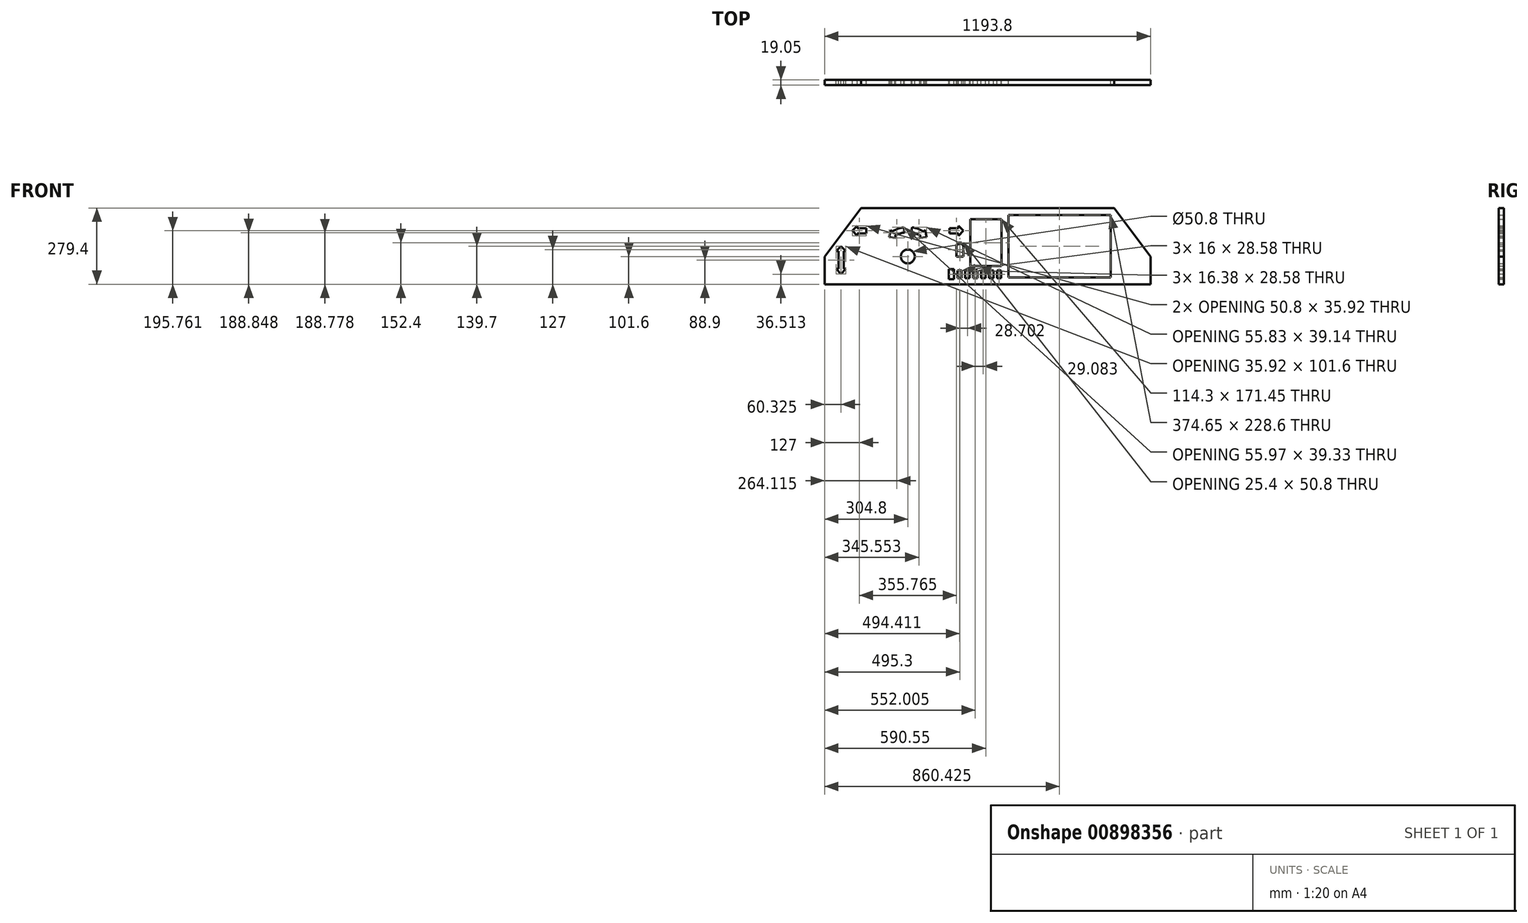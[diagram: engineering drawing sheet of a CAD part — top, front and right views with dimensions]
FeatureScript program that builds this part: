
annotation { "Feature Type Name" : "Feature", "Feature Type Description" : "" }
export const myFeature = defineFeature(function(context is Context, id is Id, definition is map)
    precondition{}
    {
        {
            var Q0;
            Q0=qCreatedBy(makeId("Front.planeOp"),FACE);
            var sketch = newSketch(context, id + "F0", { "sketchPlane" : qUnion([Q0])});
            skPoint(sketch, "E0.middle", {"position": v(0, 0) * mm});
            skLineSegment(sketch, "E1", {"start": v(-596.9, -127) * mm, "end": v(-596.9, -50.8) * mm});
            skCircle(sketch, "E2", {"center": v(-292.1, -50.8) * mm, "radius": 25.4 * mm});
            skLineSegment(sketch, "E3", {"start": v(596.9, -127) * mm, "end": v(596.9, -50.8) * mm});
            skLineSegment(sketch, "E4", {"start": v(-444.5, 52.89) * mm, "end": v(-444.5, 33.84) * mm});
            skLineSegment(sketch, "E5", {"start": v(-495.3, 43.36) * mm, "end": v(-477.34, 25.4) * mm});
            skLineSegment(sketch, "E6", {"start": v(-495.3, 43.36) * mm, "end": v(-477.34, 61.32) * mm});
            skLineSegment(sketch, "E7", {"start": v(-444.5, 52.89) * mm, "end": v(-477.34, 52.89) * mm});
            skLineSegment(sketch, "E8", {"start": v(-444.5, 33.84) * mm, "end": v(-477.34, 33.84) * mm});
            skLineSegment(sketch, "E9", {"start": v(-477.34, 52.89) * mm, "end": v(-477.34, 61.32) * mm});
            skLineSegment(sketch, "E10", {"start": v(-477.34, 25.4) * mm, "end": v(-477.34, 33.84) * mm});
            skLineSegment(sketch, "E11", {"start": v(-139.53, 52.89) * mm, "end": v(-139.53, 33.84) * mm});
            skLineSegment(sketch, "E12", {"start": v(-88.73, 43.36) * mm, "end": v(-106.7, 61.32) * mm});
            skLineSegment(sketch, "E13", {"start": v(-88.73, 43.36) * mm, "end": v(-106.7, 25.4) * mm});
            skLineSegment(sketch, "E14", {"start": v(-139.53, 52.89) * mm, "end": v(-106.7, 52.89) * mm});
            skLineSegment(sketch, "E15", {"start": v(-139.53, 33.84) * mm, "end": v(-106.7, 33.84) * mm});
            skLineSegment(sketch, "E16", {"start": v(-106.7, 33.84) * mm, "end": v(-106.7, 25.4) * mm});
            skLineSegment(sketch, "E17", {"start": v(-106.7, 52.89) * mm, "end": v(-106.7, 61.32) * mm});
            skLineSegment(sketch, "E18.left", {"start": v(76.2, -127) * mm, "end": v(76.2, 101.6) * mm});
            skLineSegment(sketch, "E19", {"start": v(596.9, -50.8) * mm, "end": v(596.9, -152.4) * mm});
            skLineSegment(sketch, "E20", {"start": v(-596.9, -50.8) * mm, "end": v(-596.9, -152.4) * mm});
            skLineSegment(sketch, "E21", {"start": v(-596.9, -152.4) * mm, "end": v(596.9, -152.4) * mm});
            skLineSegment(sketch, "E22.bottom", {"start": v(-114.3, -50.8) * mm, "end": v(-88.9, -50.8) * mm});
            skLineSegment(sketch, "E23", {"start": v(-114.3, -6.35) * mm, "end": v(-107.95, -6.35) * mm});
            skLineSegment(sketch, "E24", {"start": v(-107.95, -6.35) * mm, "end": v(-107.95, 0) * mm});
            skLineSegment(sketch, "E25", {"start": v(-114.3, -6.35) * mm, "end": v(-114.3, -50.8) * mm});
            skLineSegment(sketch, "E26", {"start": v(-88.9, -6.35) * mm, "end": v(-95.25, -6.35) * mm});
            skLineSegment(sketch, "E27", {"start": v(-95.25, -6.35) * mm, "end": v(-95.25, 0) * mm});
            skLineSegment(sketch, "E28", {"start": v(-95.25, 0) * mm, "end": v(-107.95, 0) * mm});
            skLineSegment(sketch, "E29", {"start": v(-88.9, -6.35) * mm, "end": v(-88.9, -50.8) * mm});
            skLineSegment(sketch, "E30", {"start": v(-307.52, 56.04) * mm, "end": v(-304.8, 37.19) * mm});
            skLineSegment(sketch, "E31", {"start": v(-276.51, 56.02) * mm, "end": v(-279.26, 37.17) * mm});
            skArc(sketch, "E32", {"start": v(-350.83, 39.78) * mm, "mid": v(-330.06, 50.26) * mm, "end": v(-307.52, 56.04) * mm});
            skArc(sketch, "E33", {"start": v(-340.47, 23.8) * mm, "mid": v(-323.36, 32.42) * mm, "end": v(-304.8, 37.19) * mm});
            skArc(sketch, "E34", {"start": v(-233.37, 39.78) * mm, "mid": v(-254.06, 50.23) * mm, "end": v(-276.51, 56.02) * mm});
            skArc(sketch, "E35", {"start": v(-243.73, 23.8) * mm, "mid": v(-260.78, 32.4) * mm, "end": v(-279.26, 37.17) * mm});
            skLineSegment(sketch, "E36", {"start": v(-350.83, 39.78) * mm, "end": v(-355.42, 46.85) * mm});
            skLineSegment(sketch, "E37", {"start": v(-355.42, 46.85) * mm, "end": v(-340.47, 23.8) * mm});
            skLineSegment(sketch, "E38", {"start": v(-340.47, 23.8) * mm, "end": v(-335.88, 16.71) * mm});
            skLineSegment(sketch, "E39", {"start": v(-233.37, 39.78) * mm, "end": v(-228.78, 46.85) * mm});
            skLineSegment(sketch, "E40", {"start": v(-243.73, 23.8) * mm, "end": v(-248.56, 16.88) * mm});
            skLineSegment(sketch, "E41", {"start": v(-355.42, 46.85) * mm, "end": v(-360.77, 19.71) * mm});
            skLineSegment(sketch, "E42", {"start": v(-360.77, 19.71) * mm, "end": v(-335.88, 16.71) * mm});
            skLineSegment(sketch, "E43", {"start": v(-228.78, 46.85) * mm, "end": v(-223.43, 19.71) * mm});
            skLineSegment(sketch, "E44", {"start": v(-223.43, 19.71) * mm, "end": v(-248.56, 16.88) * mm});
            skLineSegment(sketch, "E45", {"start": v(-536.58, -114.3) * mm, "end": v(-518.61, -96.34) * mm});
            skLineSegment(sketch, "E46", {"start": v(-536.58, -114.3) * mm, "end": v(-554.54, -96.34) * mm});
            skLineSegment(sketch, "E47", {"start": v(-536.58, -12.7) * mm, "end": v(-554.54, -30.66) * mm});
            skLineSegment(sketch, "E48", {"start": v(-536.58, -12.7) * mm, "end": v(-518.61, -30.66) * mm});
            skLineSegment(sketch, "E49", {"start": v(-546.1, -63.5) * mm, "end": v(-546.1, -96.34) * mm});
            skLineSegment(sketch, "E50", {"start": v(-546.1, -30.66) * mm, "end": v(-546.1, -63.5) * mm});
            skLineSegment(sketch, "E51", {"start": v(-546.1, -30.66) * mm, "end": v(-554.54, -30.66) * mm});
            skLineSegment(sketch, "E52", {"start": v(-546.1, -96.34) * mm, "end": v(-554.54, -96.34) * mm});
            skLineSegment(sketch, "E53", {"start": v(-527.05, -63.5) * mm, "end": v(-527.05, -96.34) * mm});
            skLineSegment(sketch, "E54", {"start": v(-527.05, -96.34) * mm, "end": v(-527.05, -30.66) * mm});
            skLineSegment(sketch, "E55", {"start": v(-527.05, -30.66) * mm, "end": v(-527.05, -96.34) * mm});
            skLineSegment(sketch, "E56", {"start": v(-527.05, -30.66) * mm, "end": v(-518.61, -30.66) * mm});
            skLineSegment(sketch, "E57", {"start": v(-527.05, -96.34) * mm, "end": v(-518.61, -96.34) * mm});
            skLineSegment(sketch, "E58", {"start": v(-65.79, -130.17) * mm, "end": v(-65.79, -101.6) * mm});
            skLineSegment(sketch, "E59.bottom", {"start": v(-65.79, -130.17) * mm, "end": v(-81.79, -130.17) * mm});
            skLineSegment(sketch, "E59.top", {"start": v(-65.79, -101.6) * mm, "end": v(-81.79, -101.6) * mm});
            skLineSegment(sketch, "E59.right", {"start": v(-81.79, -130.17) * mm, "end": v(-81.79, -101.6) * mm});
            skLineSegment(sketch, "E60", {"start": v(-94.49, -101.6) * mm, "end": v(-110.5, -101.6) * mm});
            skLineSegment(sketch, "E61.bottom", {"start": v(-110.5, -101.6) * mm, "end": v(-94.49, -101.6) * mm});
            skLineSegment(sketch, "E61.top", {"start": v(-110.5, -130.17) * mm, "end": v(-94.49, -130.17) * mm});
            skLineSegment(sketch, "E61.left", {"start": v(-110.5, -101.6) * mm, "end": v(-110.5, -130.17) * mm});
            skLineSegment(sketch, "E61.right", {"start": v(-94.49, -101.6) * mm, "end": v(-94.49, -130.17) * mm});
            skLineSegment(sketch, "E62.right", {"start": v(-123.2, -101.6) * mm, "end": v(-123.2, -130.17) * mm});
            skLineSegment(sketch, "E63", {"start": v(-596.9, -50.8) * mm, "end": v(-463.55, 127) * mm});
            skLineSegment(sketch, "E64", {"start": v(596.9, -50.8) * mm, "end": v(463.55, 127) * mm});
            skLineSegment(sketch, "E65", {"start": v(463.55, 127) * mm, "end": v(-463.55, 127) * mm});
            skLineSegment(sketch, "E66", {"start": v(50.8, -85.72) * mm, "end": v(-63.5, -85.73) * mm});
            skLineSegment(sketch, "E67", {"start": v(-63.5, -85.73) * mm, "end": v(-63.5, 85.73) * mm});
            skLineSegment(sketch, "E68", {"start": v(-63.5, 85.73) * mm, "end": v(50.8, 85.73) * mm});
            skLineSegment(sketch, "E69", {"start": v(50.8, 85.72) * mm, "end": v(50.8, -85.72) * mm});
            skLineSegment(sketch, "E70", {"start": v(450.85, 0) * mm, "end": v(450.85, 101.6) * mm});
            skLineSegment(sketch, "E71.bottom", {"start": v(450.85, 101.6) * mm, "end": v(76.2, 101.6) * mm});
            skLineSegment(sketch, "E71.top", {"start": v(450.85, -127) * mm, "end": v(76.2, -127) * mm});
            skLineSegment(sketch, "E71.left", {"start": v(450.85, 101.6) * mm, "end": v(450.85, -127) * mm});
            skLineSegment(sketch, "E71.right", {"start": v(76.2, 101.6) * mm, "end": v(76.2, -127) * mm});
            skLineSegment(sketch, "E72.bottom", {"start": v(-53.09, -101.6) * mm, "end": v(-36.7, -101.6) * mm});
            skLineSegment(sketch, "E72.top", {"start": v(-53.09, -130.17) * mm, "end": v(-36.7, -130.17) * mm});
            skLineSegment(sketch, "E72.left", {"start": v(-53.09, -101.6) * mm, "end": v(-53.09, -130.17) * mm});
            skLineSegment(sketch, "E72.right", {"start": v(-36.7, -101.6) * mm, "end": v(-36.7, -130.17) * mm});
            skLineSegment(sketch, "E73.bottom", {"start": v(-24, -101.6) * mm, "end": v(-7.62, -101.6) * mm});
            skLineSegment(sketch, "E73.top", {"start": v(-24, -130.17) * mm, "end": v(-7.62, -130.17) * mm});
            skLineSegment(sketch, "E73.left", {"start": v(-24, -101.6) * mm, "end": v(-24, -130.17) * mm});
            skLineSegment(sketch, "E73.right", {"start": v(-7.62, -101.6) * mm, "end": v(-7.62, -130.17) * mm});
            skLineSegment(sketch, "E74.bottom", {"start": v(5.08, -101.6) * mm, "end": v(21.46, -101.6) * mm});
            skLineSegment(sketch, "E74.top", {"start": v(5.08, -130.17) * mm, "end": v(21.46, -130.17) * mm});
            skLineSegment(sketch, "E74.left", {"start": v(5.08, -101.6) * mm, "end": v(5.08, -130.17) * mm});
            skLineSegment(sketch, "E74.right", {"start": v(21.46, -101.6) * mm, "end": v(21.46, -130.17) * mm});
            skLineSegment(sketch, "E75.bottom", {"start": v(-81.79, -101.6) * mm, "end": v(-65.79, -101.6) * mm});
            skLineSegment(sketch, "E75.top", {"start": v(-81.79, -130.17) * mm, "end": v(-65.79, -130.17) * mm});
            skLineSegment(sketch, "E75.left", {"start": v(-81.79, -101.6) * mm, "end": v(-81.79, -130.17) * mm});
            skLineSegment(sketch, "E75.right", {"start": v(-65.79, -101.6) * mm, "end": v(-65.79, -130.17) * mm});
            skLineSegment(sketch, "E76", {"start": v(-123.2, -115.89) * mm, "end": v(-123.2, -134.22) * mm});
            skLineSegment(sketch, "E77", {"start": v(-123.2, -115.89) * mm, "end": v(-123.2, -97.55) * mm});
            skLineSegment(sketch, "E78", {"start": v(-123.2, -97.55) * mm, "end": v(-142.2, -97.55) * mm});
            skLineSegment(sketch, "E79.bottom", {"start": v(-142.2, -97.55) * mm, "end": v(-123.2, -97.55) * mm});
            skLineSegment(sketch, "E79.top", {"start": v(-142.2, -134.22) * mm, "end": v(-123.2, -134.22) * mm});
            skLineSegment(sketch, "E79.left", {"start": v(-142.2, -97.55) * mm, "end": v(-142.2, -134.22) * mm});
            skLineSegment(sketch, "E79.right", {"start": v(-123.2, -97.55) * mm, "end": v(-123.2, -134.22) * mm});
            skLineSegment(sketch, "E80.bottom", {"start": v(34.16, -101.6) * mm, "end": v(50.17, -101.6) * mm});
            skLineSegment(sketch, "E80.top", {"start": v(34.16, -130.17) * mm, "end": v(50.17, -130.17) * mm});
            skLineSegment(sketch, "E80.left", {"start": v(34.16, -101.6) * mm, "end": v(34.16, -130.17) * mm});
            skLineSegment(sketch, "E80.right", {"start": v(50.17, -101.6) * mm, "end": v(50.17, -130.17) * mm});
            skSolve(sketch);
        }
        {
            var Q0;
            Q0=makeQuery(id+"F0.imprint","IMPRINT",FACE,{"disambiguationData":[TD([[makeQuery(id+"F0.imprint","IMPRINT",EDGE,{"derivedFrom":sQuery(id+"F0.wireOp",EDGE,"E2")}),-1.0]])]});
            extrude(context, id + "F1", {"entities" : qUnion([Q0]), "depth" : 19.05 * mm, "offsetDistance" : 25.4 * mm});
        }
    });
